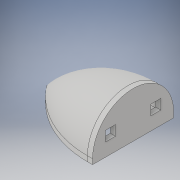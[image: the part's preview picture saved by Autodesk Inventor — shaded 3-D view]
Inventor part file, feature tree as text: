
AUTODESK INVENTOR PART (.ipt)
format: ipt  version: 2019 (Build 230136000, 136)  size: 185,856 bytes
history: native  units: in
note: dims shown in document units (in); Inventor stores cm internally (conversion verified against a paired STEP export)
features: extrude x2, sketch x2, projected_geometry x2, revolve x1
ambient origin geometry x8: Origin, YZ Plane, XZ Plane, XY Plane, X Axis, Y Axis, Z Axis, Center Point
bodies: Solid1 (feature_tree)
feature tree (7):
  revolve  "Revolution1"  [1 undecoded]
  extrude  "Extrusion2"  Depth=3.9449in
  extrude  "Extrusion3"  TaperAngle=180.0deg  [1 undecoded]
  sketch  "Sketch3"  dims[d13=0.25in d15=1.9724in]
  sketch  "Sketch4"  dims[d16=0.25in d17=3.9449in d18=180.0deg d21=2.0in d23=1.0in d24=0.25in d26=0.25in d27=0.0in d28=0.4924in d29=0.4924in d30=0.8576in d31=0.25in d32=0.0in]
  projected_geometry  "Projected Loop1"
  projected_geometry  "Projected Loop2"
note: 2 required parameter values undecoded (feature->parameter linkage not recoverable at this tier; creation-order binding heuristic only, values carry confidence <= 0.55)